# Revit family: Запорный клапан 4218 AGF
name_source: partatom
category: Rohrzubehör
revit_build: Autodesk Revit 2018 (Build: 20190510_1515(x64)
units: mm (PartAtom-declared; Revit-internal decimal feet)

## family parameters
Arbeitsebenenbasiert = Nein
Beim Laden mit Abzugskörper schneiden = Nein
Bemaßung runder Anschluss = Durchmesser verwenden
Gemeinsam genutzt = Nein
Immer vertikal = Ja
Teiletyp = Unterbricht

## types (1)
- Запорный клапан 4218 AGF
    Hersteller = HERZ-Armaturen Ges.m.b.H
    O-Ringe = EPDM
    PN = 16
    SCRNCODE = 05;11;2
    SCRNSEQ = ARM;ARM_TYP="ABSV";2
    URL = www.herz-armaturen.ru
    w = 10.00°
    Букса для клапана = Латунь
    Корпус = Серый чугун GJL 250 в соответствии с EN 1561
    Макс. рабочая температура до DN32 = 130 °C
    Макс. рабочая температура с DN40 = 110 °C
    Макс. рабочее давление = 1600000.0 Pa
    Область применения = Для гидравлической балансировки в системах отопления или холодоснабжения, регулирования и перекрытия трубопроводов, стояков, теплообменников, регистров отопления и охлаждения.
    Среда = Качество теплоносителя в соответствии с ÖNORM H5195 и/или предписаниями VDI 2035.
Разрешается использование смеси этилен или пропиленгликоля в соотношении 25-50% с водой.
